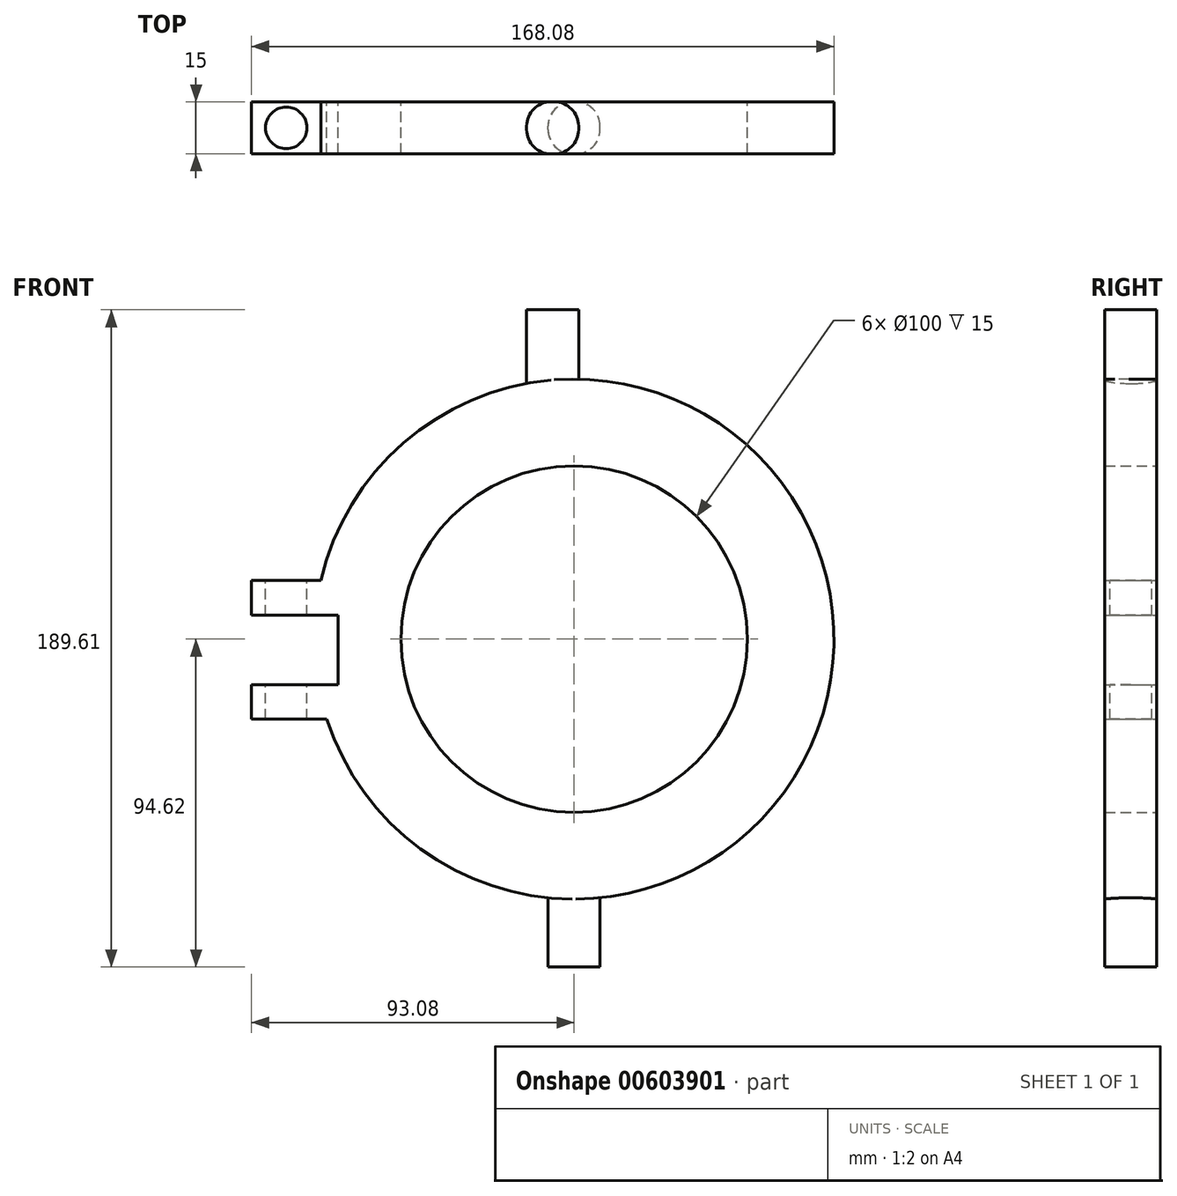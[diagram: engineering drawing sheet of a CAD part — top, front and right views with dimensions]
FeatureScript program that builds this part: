
annotation { "Feature Type Name" : "Feature", "Feature Type Description" : "" }
export const myFeature = defineFeature(function(context is Context, id is Id, definition is map)
    precondition{}
    {
        {
            var Q0;
            Q0=qCreatedBy(makeId("Front.planeOp"),FACE);
            var sketch = newSketch(context, id + "F0", { "sketchPlane" : qUnion([Q0])});
            skCircle(sketch, "E0", {"center": v(0, 0) * mm, "radius": 50 * mm});
            skArc(sketch, "E1", {"start": v(-13.7, 73.74) * mm, "mid": v(-51.87, 54.17) * mm, "end": v(-73.08, 16.87) * mm});
            skLineSegment(sketch, "E2", {"start": v(-6.2, 94.99) * mm, "end": v(1.3, 94.99) * mm});
            skLineSegment(sketch, "E3", {"start": v(1.3, 94.99) * mm, "end": v(1.3, 74.99) * mm});
            skLineSegment(sketch, "E4", {"start": v(-6.2, 94.99) * mm, "end": v(-13.7, 94.99) * mm});
            skLineSegment(sketch, "E5", {"start": v(-13.7, 94.99) * mm, "end": v(-13.7, 73.74) * mm});
            skLineSegment(sketch, "E6", {"start": v(0, -94.62) * mm, "end": v(7.5, -94.62) * mm});
            skLineSegment(sketch, "E7", {"start": v(7.5, -94.62) * mm, "end": v(7.5, -74.62) * mm});
            skLineSegment(sketch, "E8", {"start": v(0, -94.62) * mm, "end": v(-7.5, -94.62) * mm});
            skLineSegment(sketch, "E9", {"start": v(-7.5, -94.62) * mm, "end": v(-7.5, -74.62) * mm});
            skPoint(sketch, "E10.start.orphan", {"position": v(0, 75) * mm});
            skPoint(sketch, "E11.start.orphan", {"position": v(0, -75) * mm});
            skArc(sketch, "E12.trimOffspring", {"start": v(7.5, -74.62) * mm, "mid": v(74.94, 3.1) * mm, "end": v(1.3, 74.99) * mm});
            skPoint(sketch, "E13.endSnap0", {"position": v(-74.93, -3.13) * mm});
            skLineSegment(sketch, "E14", {"start": v(-93.08, 6.87) * mm, "end": v(-93.08, 16.87) * mm});
            skLineSegment(sketch, "E15", {"start": v(-93.08, 16.87) * mm, "end": v(-73.08, 16.87) * mm});
            skLineSegment(sketch, "E16", {"start": v(-93.08, -13.13) * mm, "end": v(-93.08, -23.13) * mm});
            skLineSegment(sketch, "E17", {"start": v(-93.08, -23.13) * mm, "end": v(-71.34, -23.13) * mm});
            skArc(sketch, "E18.trimOffspring", {"start": v(-71.34, -23.13) * mm, "mid": v(-47.09, -58.38) * mm, "end": v(-7.5, -74.62) * mm});
            skLineSegment(sketch, "E19", {"start": v(-93.08, 6.87) * mm, "end": v(-68.08, 6.87) * mm});
            skLineSegment(sketch, "E20", {"start": v(-68.08, 6.87) * mm, "end": v(-68.08, -13.13) * mm});
            skLineSegment(sketch, "E21", {"start": v(-68.08, -13.13) * mm, "end": v(-93.08, -13.13) * mm});
            skPoint(sketch, "E22.orphan", {"position": v(-93.08, -3.13) * mm});
            skSolve(sketch);
        }
        {
            var Q0;
            Q0=makeQuery(id+"F0.imprint","IMPRINT",FACE,{"disambiguationData":[TD([[makeQuery(id+"F0.imprint","IMPRINT",EDGE,{"derivedFrom":sQuery(id+"F0.wireOp",EDGE,"E0")}),-1.0]])]});
            extrude(context, id + "F1", {"entities" : qUnion([Q0]), "depth" : 15 * mm, "offsetDistance" : 25 * mm});
        }
        {
            var Q0;
            Q0=makeQuery(id+"F1.opExtrude","CAP_EDGE",EDGE,{"disambiguationData":[OSD([sQuery(id+"F0.wireOp",EDGE,"E9")])],"isStart":false});
            var Q1;
            Q1=makeQuery(id+"F1.opExtrude","CAP_EDGE",EDGE,{"disambiguationData":[OSD([sQuery(id+"F0.wireOp",EDGE,"E7")])],"isStart":false});
            var Q2;
            Q2=makeQuery(id+"F1.opExtrude","CAP_EDGE",EDGE,{"disambiguationData":[OSD([sQuery(id+"F0.wireOp",EDGE,"E7")])],"isStart":true});
            var Q3;
            Q3=makeQuery(id+"F1.opExtrude","CAP_EDGE",EDGE,{"disambiguationData":[OSD([sQuery(id+"F0.wireOp",EDGE,"E9")])],"isStart":true});
            fillet(context, id + "F2", {"entities" : qUnion([Q0, Q1, Q2, Q3]), "radius" : 7 * mm, "tangentPropagation" : true, "allowEdgeOverflow" : false});
        }
        {
            var Q0;
            Q0=makeQuery(id+"F1.opExtrude","CAP_EDGE",EDGE,{"disambiguationData":[OSD([sQuery(id+"F0.wireOp",EDGE,"E3")])],"isStart":false});
            var Q1;
            Q1=makeQuery(id+"F1.opExtrude","CAP_EDGE",EDGE,{"disambiguationData":[OSD([sQuery(id+"F0.wireOp",EDGE,"E3")])],"isStart":true});
            var Q2;
            Q2=makeQuery(id+"F1.opExtrude","CAP_EDGE",EDGE,{"disambiguationData":[OSD([sQuery(id+"F0.wireOp",EDGE,"E5")])],"isStart":false});
            var Q3;
            Q3=makeQuery(id+"F1.opExtrude","CAP_EDGE",EDGE,{"disambiguationData":[OSD([sQuery(id+"F0.wireOp",EDGE,"E5")])],"isStart":true});
            fillet(context, id + "F3", {"entities" : qUnion([Q0, Q1, Q2, Q3]), "radius" : 7 * mm, "tangentPropagation" : true, "allowEdgeOverflow" : false});
        }
        {
            var Q0;
            Q0=makeQuery(id+"F1.opExtrude","SWEPT_FACE",FACE,{"disambiguationData":[OSD([sQuery(id+"F0.wireOp",EDGE,"E15")])]});
            var sketch = newSketch(context, id + "F4", { "sketchPlane" : qUnion([Q0])});
            skLineSegment(sketch, "E23", {"start": v(-93.08, -7.5) * mm, "end": v(-83.08, -7.5) * mm});
            skCircle(sketch, "E24", {"center": v(-83.08, -7.5) * mm, "radius": 6 * mm});
            skSolve(sketch);
        }
        {
            var Q0;
            Q0 = qSketchRegion(id + "F4", true);
            extrude(context, id + "F5", {"entities" : qUnion([Q0]), "operationType" : NewBodyOperationType.REMOVE, "oppositeDirection" : true, "depth" : 42.6 * mm, "offsetDistance" : 25 * mm});
        }
    });
